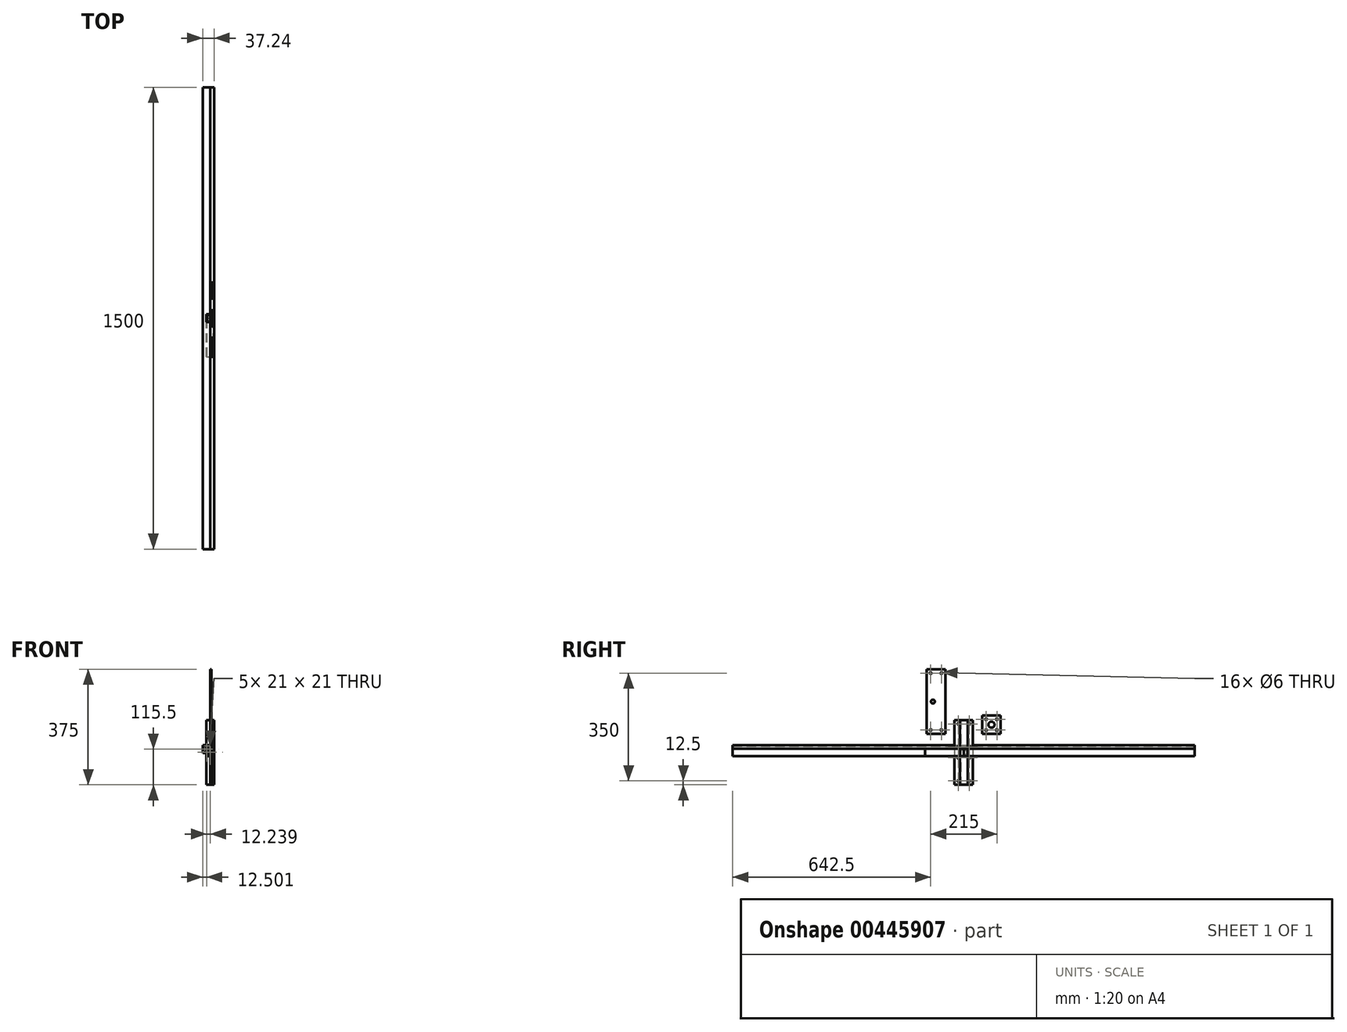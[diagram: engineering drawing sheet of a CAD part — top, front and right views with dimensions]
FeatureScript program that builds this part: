
annotation { "Feature Type Name" : "Feature", "Feature Type Description" : "" }
export const myFeature = defineFeature(function(context is Context, id is Id, definition is map)
    precondition{}
    {
        {
            var Q0;
            Q0=qCreatedBy(makeId("Front.planeOp"),FACE);
            var sketch = newSketch(context, id + "F0", { "sketchPlane" : qUnion([Q0])});
            skLineSegment(sketch, "E0.bottom", {"start": v(-10.5, 10.5) * mm, "end": v(10.5, 10.5) * mm});
            skLineSegment(sketch, "E0.top", {"start": v(-10.5, -10.5) * mm, "end": v(10.5, -10.5) * mm});
            skLineSegment(sketch, "E0.left", {"start": v(-10.5, 10.5) * mm, "end": v(-10.5, -10.5) * mm});
            skLineSegment(sketch, "E0.right", {"start": v(10.5, 10.5) * mm, "end": v(10.5, -10.5) * mm});
            skPoint(sketch, "E0.middle", {"position": v(0, 0) * mm});
            skLineSegment(sketch, "E1.bottom", {"start": v(-12.5, 12.5) * mm, "end": v(12.5, 12.5) * mm});
            skLineSegment(sketch, "E1.top", {"start": v(-12.5, -12.5) * mm, "end": v(12.5, -12.5) * mm});
            skLineSegment(sketch, "E1.left", {"start": v(-12.5, 12.5) * mm, "end": v(-12.5, -12.5) * mm});
            skLineSegment(sketch, "E1.right", {"start": v(12.5, 12.5) * mm, "end": v(12.5, -12.5) * mm});
            skSolve(sketch);
        }
        {
            var Q0;
            Q0 = qSketchRegion(id + "F0", true);
            extrude(context, id + "F1", {"entities" : qUnion([Q0]), "endBound" : BoundingType.SYMMETRIC, "depth" : 1500 * mm});
        }
        {
            var Q0;
            Q0=qCreatedBy(makeId("Front.planeOp"),FACE);
            var sketch = newSketch(context, id + "F2", { "sketchPlane" : qUnion([Q0])});
            skLineSegment(sketch, "E2.bottom", {"start": v(10.5, 10.5) * mm, "end": v(-10.5, 10.5) * mm});
            skLineSegment(sketch, "E2.top", {"start": v(10.5, -10.5) * mm, "end": v(-10.5, -10.5) * mm});
            skLineSegment(sketch, "E2.left", {"start": v(10.5, 10.5) * mm, "end": v(10.5, -10.5) * mm});
            skLineSegment(sketch, "E2.right", {"start": v(-10.5, 10.5) * mm, "end": v(-10.5, -10.5) * mm});
            skPoint(sketch, "E2.middle", {"position": v(0, 0) * mm});
            skLineSegment(sketch, "E3.bottom", {"start": v(12.5, 12.5) * mm, "end": v(-12.5, 12.5) * mm});
            skLineSegment(sketch, "E3.top", {"start": v(12.5, -12.5) * mm, "end": v(-12.5, -12.5) * mm});
            skLineSegment(sketch, "E3.left", {"start": v(12.5, 12.5) * mm, "end": v(12.5, -12.5) * mm});
            skLineSegment(sketch, "E3.right", {"start": v(-12.5, 12.5) * mm, "end": v(-12.5, -12.5) * mm});
            skSolve(sketch);
        }
        {
            var Q0;
            Q0 = qSketchRegion(id + "F2", true);
            extrude(context, id + "F3", {"entities" : qUnion([Q0]), "endBound" : BoundingType.SYMMETRIC, "depth" : 1500 * mm});
        }
        {
            var Q0;
            Q0=qCreatedBy(makeId("Front.planeOp"),FACE);
            var sketch = newSketch(context, id + "F4", { "sketchPlane" : qUnion([Q0])});
            skLineSegment(sketch, "E4.bottom", {"start": v(-22.74, 0) * mm, "end": v(-1.74, 0) * mm});
            skLineSegment(sketch, "E4.top", {"start": v(-22.74, 21) * mm, "end": v(-1.74, 21) * mm});
            skLineSegment(sketch, "E4.left", {"start": v(-22.74, 0) * mm, "end": v(-22.74, 21) * mm});
            skLineSegment(sketch, "E4.right", {"start": v(-1.74, 0) * mm, "end": v(-1.74, 21) * mm});
            skPoint(sketch, "E4.middle", {"position": v(-12.24, 10.5) * mm});
            skLineSegment(sketch, "E5.bottom", {"start": v(-24.74, 23) * mm, "end": v(0.26, 23) * mm});
            skLineSegment(sketch, "E5.top", {"start": v(-24.74, -2) * mm, "end": v(0.26, -2) * mm});
            skLineSegment(sketch, "E5.left", {"start": v(-24.74, 23) * mm, "end": v(-24.74, -2) * mm});
            skLineSegment(sketch, "E5.right", {"start": v(0.26, 23) * mm, "end": v(0.26, -2) * mm});
            skSolve(sketch);
        }
        {
            var Q0;
            Q0 = qSketchRegion(id + "F4", true);
            extrude(context, id + "F5", {"entities" : qUnion([Q0]), "endBound" : BoundingType.SYMMETRIC, "depth" : 1500 * mm});
        }
        {
            var Q0;
            Q0=qCreatedBy(makeId("Front.planeOp"),FACE);
            var sketch = newSketch(context, id + "F6", { "sketchPlane" : qUnion([Q0])});
            skLineSegment(sketch, "E6.bottom", {"start": v(10.5, -10.5) * mm, "end": v(-10.5, -10.5) * mm});
            skLineSegment(sketch, "E6.top", {"start": v(10.5, 10.5) * mm, "end": v(-10.5, 10.5) * mm});
            skLineSegment(sketch, "E6.left", {"start": v(10.5, -10.5) * mm, "end": v(10.5, 10.5) * mm});
            skLineSegment(sketch, "E6.right", {"start": v(-10.5, -10.5) * mm, "end": v(-10.5, 10.5) * mm});
            skPoint(sketch, "E6.middle", {"position": v(0, 0) * mm});
            skLineSegment(sketch, "E7.bottom", {"start": v(12.5, -12.5) * mm, "end": v(-12.5, -12.5) * mm});
            skLineSegment(sketch, "E7.top", {"start": v(12.5, 12.5) * mm, "end": v(-12.5, 12.5) * mm});
            skLineSegment(sketch, "E7.left", {"start": v(12.5, -12.5) * mm, "end": v(12.5, 12.5) * mm});
            skLineSegment(sketch, "E7.right", {"start": v(-12.5, -12.5) * mm, "end": v(-12.5, 12.5) * mm});
            skSolve(sketch);
        }
        {
            var Q0;
            Q0 = qSketchRegion(id + "F6", true);
            extrude(context, id + "F7", {"entities" : qUnion([Q0]), "endBound" : BoundingType.SYMMETRIC, "depth" : 1500 * mm});
        }
        {
            var Q0;
            Q0=qCreatedBy(makeId("Top.planeOp"),FACE);
            var sketch = newSketch(context, id + "F8", { "sketchPlane" : qUnion([Q0])});
            skLineSegment(sketch, "E8.bottom", {"start": v(10.5, 10.5) * mm, "end": v(-10.5, 10.5) * mm});
            skLineSegment(sketch, "E8.top", {"start": v(10.5, -10.5) * mm, "end": v(-10.5, -10.5) * mm});
            skLineSegment(sketch, "E8.left", {"start": v(10.5, 10.5) * mm, "end": v(10.5, -10.5) * mm});
            skLineSegment(sketch, "E8.right", {"start": v(-10.5, 10.5) * mm, "end": v(-10.5, -10.5) * mm});
            skPoint(sketch, "E8.middle", {"position": v(0, 0) * mm});
            skLineSegment(sketch, "E9.bottom", {"start": v(12.5, 12.5) * mm, "end": v(-12.5, 12.5) * mm});
            skLineSegment(sketch, "E9.top", {"start": v(12.5, -12.5) * mm, "end": v(-12.5, -12.5) * mm});
            skLineSegment(sketch, "E9.left", {"start": v(12.5, 12.5) * mm, "end": v(12.5, -12.5) * mm});
            skLineSegment(sketch, "E9.right", {"start": v(-12.5, 12.5) * mm, "end": v(-12.5, -12.5) * mm});
            skSolve(sketch);
        }
        {
            var Q0;
            Q0 = qSketchRegion(id + "F8", true);
            extrude(context, id + "F9", {"entities" : qUnion([Q0]), "endBound" : BoundingType.SYMMETRIC, "depth" : 210 * mm});
        }
        {
            var Q0;
            Q0=qCreatedBy(makeId("Right.planeOp"),FACE);
            var sketch = newSketch(context, id + "F10", { "sketchPlane" : qUnion([Q0])});
            skPoint(sketch, "E10", {"position": v(-72.5, 72.5) * mm});
            skPoint(sketch, "E11", {"position": v(-107.5, 72.5) * mm});
            skPoint(sketch, "E12", {"position": v(-107.5, 257.5) * mm});
            skPoint(sketch, "E13", {"position": v(-100, 165) * mm});
            skPoint(sketch, "E14", {"position": v(-72.5, 257.5) * mm});
            skLineSegment(sketch, "E15.bottom", {"start": v(-60, 60) * mm, "end": v(-120, 60) * mm});
            skLineSegment(sketch, "E15.top", {"start": v(-60, 270) * mm, "end": v(-120, 270) * mm});
            skLineSegment(sketch, "E15.left", {"start": v(-60, 60) * mm, "end": v(-60, 270) * mm});
            skLineSegment(sketch, "E15.right", {"start": v(-120, 60) * mm, "end": v(-120, 270) * mm});
            skCircle(sketch, "E16", {"center": v(-107.5, 257.5) * mm, "radius": 3 * mm});
            skCircle(sketch, "E17", {"center": v(-72.5, 257.5) * mm, "radius": 3 * mm});
            skCircle(sketch, "E18", {"center": v(-107.5, 72.5) * mm, "radius": 3 * mm});
            skCircle(sketch, "E19", {"center": v(-72.5, 72.5) * mm, "radius": 3 * mm});
            skCircle(sketch, "E20", {"center": v(-100, 165) * mm, "radius": 6.25 * mm});
            skSolve(sketch);
        }
        {
            var Q0;
            Q0 = qSketchRegion(id + "F10", true);
            extrude(context, id + "F11", {"entities" : qUnion([Q0]), "depth" : 3 * mm});
        }
        {
            var Q0;
            Q0=qCreatedBy(makeId("Right.planeOp"),FACE);
            var sketch = newSketch(context, id + "F12", { "sketchPlane" : qUnion([Q0])});
            skLineSegment(sketch, "E21.bottom", {"start": v(60, 60) * mm, "end": v(120, 60) * mm});
            skLineSegment(sketch, "E21.top", {"start": v(60, 120) * mm, "end": v(120, 120) * mm});
            skLineSegment(sketch, "E21.left", {"start": v(60, 60) * mm, "end": v(60, 120) * mm});
            skLineSegment(sketch, "E21.right", {"start": v(120, 60) * mm, "end": v(120, 120) * mm});
            skPoint(sketch, "E22", {"position": v(107.5, 72.5) * mm});
            skPoint(sketch, "E23", {"position": v(72.5, 107.5) * mm});
            skPoint(sketch, "E24", {"position": v(107.5, 107.5) * mm});
            skPoint(sketch, "E25", {"position": v(90, 90) * mm});
            skPoint(sketch, "E26", {"position": v(72.5, 72.5) * mm});
            skCircle(sketch, "E27", {"center": v(72.5, 107.5) * mm, "radius": 3 * mm});
            skCircle(sketch, "E28", {"center": v(107.5, 107.5) * mm, "radius": 3 * mm});
            skCircle(sketch, "E29", {"center": v(72.5, 72.5) * mm, "radius": 3 * mm});
            skCircle(sketch, "E30", {"center": v(107.5, 72.5) * mm, "radius": 3 * mm});
            skCircle(sketch, "E31", {"center": v(90, 90) * mm, "radius": 10 * mm});
            skSolve(sketch);
        }
        {
            var Q0;
            Q0 = qSketchRegion(id + "F12", true);
            extrude(context, id + "F13", {"entities" : qUnion([Q0]), "depth" : 3 * mm});
        }
        {
            var Q0;
            Q0=qCreatedBy(makeId("Right.planeOp"),FACE);
            var sketch = newSketch(context, id + "F14", { "sketchPlane" : qUnion([Q0])});
            skPoint(sketch, "E32", {"position": v(-17.5, 17.5) * mm});
            skPoint(sketch, "E33", {"position": v(17.5, 17.5) * mm});
            skPoint(sketch, "E34", {"position": v(17.5, -17.5) * mm});
            skPoint(sketch, "E35", {"position": v(-17.5, -17.5) * mm});
            skPoint(sketch, "E36", {"position": v(17.5, -92.5) * mm});
            skPoint(sketch, "E37", {"position": v(-17.5, -92.5) * mm});
            skPoint(sketch, "E38", {"position": v(-17.5, 92.5) * mm});
            skPoint(sketch, "E39", {"position": v(17.5, 92.5) * mm});
            skLineSegment(sketch, "E40.bottom", {"start": v(30, 105) * mm, "end": v(-30, 105) * mm});
            skLineSegment(sketch, "E40.top", {"start": v(30, -105) * mm, "end": v(-30, -105) * mm});
            skLineSegment(sketch, "E40.left", {"start": v(30, 105) * mm, "end": v(30, -105) * mm});
            skLineSegment(sketch, "E40.right", {"start": v(-30, 105) * mm, "end": v(-30, -105) * mm});
            skPoint(sketch, "E40.middle", {"position": v(0, 0) * mm});
            skCircle(sketch, "E41", {"center": v(-17.5, 92.5) * mm, "radius": 3 * mm});
            skCircle(sketch, "E42", {"center": v(-17.5, 17.5) * mm, "radius": 3 * mm});
            skCircle(sketch, "E43", {"center": v(17.5, 17.5) * mm, "radius": 3 * mm});
            skCircle(sketch, "E44", {"center": v(17.5, 92.5) * mm, "radius": 3 * mm});
            skCircle(sketch, "E45", {"center": v(17.5, -17.5) * mm, "radius": 3 * mm});
            skCircle(sketch, "E46", {"center": v(-17.5, -17.5) * mm, "radius": 3 * mm});
            skCircle(sketch, "E47", {"center": v(-17.5, -92.5) * mm, "radius": 3 * mm});
            skCircle(sketch, "E48", {"center": v(17.5, -92.5) * mm, "radius": 3 * mm});
            skCircle(sketch, "E49", {"center": v(0, 0) * mm, "radius": 10 * mm});
            skSolve(sketch);
        }
        {
            var Q0;
            Q0 = qSketchRegion(id + "F14", true);
            extrude(context, id + "F15", {"entities" : qUnion([Q0]), "depth" : 3 * mm});
        }
        {
            var Q0;
            Q0=qCreatedBy(makeId("Front.planeOp"),FACE);
            var sketch = newSketch(context, id + "F16", { "sketchPlane" : qUnion([Q0])});
            skLineSegment(sketch, "E50.bottom", {"start": v(-10.5, 10.5) * mm, "end": v(10.5, 10.5) * mm});
            skLineSegment(sketch, "E50.top", {"start": v(-10.5, -10.5) * mm, "end": v(10.5, -10.5) * mm});
            skLineSegment(sketch, "E50.left", {"start": v(-10.5, 10.5) * mm, "end": v(-10.5, -10.5) * mm});
            skLineSegment(sketch, "E50.right", {"start": v(10.5, 10.5) * mm, "end": v(10.5, -10.5) * mm});
            skPoint(sketch, "E50.middle", {"position": v(0, 0) * mm});
            skLineSegment(sketch, "E51.bottom", {"start": v(-12.5, 12.5) * mm, "end": v(12.5, 12.5) * mm});
            skLineSegment(sketch, "E51.top", {"start": v(-12.5, -12.5) * mm, "end": v(12.5, -12.5) * mm});
            skLineSegment(sketch, "E51.left", {"start": v(-12.5, 12.5) * mm, "end": v(-12.5, -12.5) * mm});
            skLineSegment(sketch, "E51.right", {"start": v(12.5, 12.5) * mm, "end": v(12.5, -12.5) * mm});
            skSolve(sketch);
        }
        {
            var Q0;
            Q0 = qSketchRegion(id + "F16", true);
            extrude(context, id + "F17", {"entities" : qUnion([Q0]), "depth" : 125 * mm});
        }
        {
            var Q0;
            Q0=makeQuery(id+"F17.opExtrude","SWEPT_FACE",FACE,{"disambiguationData":[OSD([sQuery(id+"F16.wireOp",EDGE,"E51.bottom")])]});
            var sketch = newSketch(context, id + "F18", { "sketchPlane" : qUnion([Q0])});
            skPoint(sketch, "E52", {"position": v(0, -211.77) * mm});
            skPoint(sketch, "E53", {"position": v(0, -12.5) * mm});
            skPoint(sketch, "E54", {"position": v(0, -112.5) * mm});
            skSolve(sketch);
        }
        {
            var Q0;
            Q0=sQuery(id+"F18.wireOp",VERTEX,"E54");
            var Q1;
            Q1=makeQuery(id+"F17.opExtrude","SWEPT_BODY",BODY,{"disambiguationData":[OSD([sQuery(id+"F16.wireOp",EDGE,"E50.bottom"),sQuery(id+"F16.wireOp",EDGE,"E50.top"),sQuery(id+"F16.wireOp",EDGE,"E50.left"),sQuery(id+"F16.wireOp",EDGE,"E50.right"),sQuery(id+"F16.wireOp",EDGE,"E51.bottom"),sQuery(id+"F16.wireOp",EDGE,"E51.top"),sQuery(id+"F16.wireOp",EDGE,"E51.left"),sQuery(id+"F16.wireOp",EDGE,"E51.right")])]});
            hole(context, id + "F19", {"style" : HoleStyle.SIMPLE, "endStyle" : HoleEndStyle.THROUGH, "holeDiameter" : 6 * mm, "isTappedThrough" : true, "tappedDepth" : 12 * mm, "tapClearance" : 3, "locations" : qUnion([Q0]), "scope" : qUnion([Q1])});
        }
        {
            var Q0;
            Q0=sQuery(id+"F18.wireOp",VERTEX,"E53");
            var Q1;
            Q1=makeQuery(id+"F17.opExtrude","SWEPT_BODY",BODY,{"disambiguationData":[OSD([sQuery(id+"F16.wireOp",EDGE,"E50.bottom"),sQuery(id+"F16.wireOp",EDGE,"E50.top"),sQuery(id+"F16.wireOp",EDGE,"E50.left"),sQuery(id+"F16.wireOp",EDGE,"E50.right"),sQuery(id+"F16.wireOp",EDGE,"E51.bottom"),sQuery(id+"F16.wireOp",EDGE,"E51.top"),sQuery(id+"F16.wireOp",EDGE,"E51.left"),sQuery(id+"F16.wireOp",EDGE,"E51.right")])]});
            hole(context, id + "F20", {"style" : HoleStyle.SIMPLE, "endStyle" : HoleEndStyle.THROUGH, "holeDiameter" : 6 * mm, "isTappedThrough" : true, "tappedDepth" : 12 * mm, "tapClearance" : 3, "locations" : qUnion([Q0]), "scope" : qUnion([Q1])});
        }
    });
